# Revit family: FT Excalibur_2021
name_source: partatom
category: Luminarias
units: mm (PartAtom-declared; Revit-internal decimal feet)

## family parameters
Compartido = No
Corte con vacíos al cargar = No
Cota de conector redondo = Diámetro de uso
Número OmniClass = 23.80.70.00
Origen de luz = Sí
Punto de cálculo de habitación = No
Se basa en plano de trabajo = No
Siempre vertical = Sí
Tipo de pieza = Normal
Título OmniClass = Lighting

## types (12) — shared parameters
Cambio de temperatura de color de luz atenuada = <Ninguno>
Chromatic Index = CR>80
Descripción = https://www.airfal.com
Emergency system = No
Filtro de color = 16777215
Glow wire test = 960ºC
IK = IK07
IP = IP67
Led Module = Sí
MacAdam Ellipse = 3/4
Photobiological risk group = RG 0/1
URL = https://www.airfal.com
Unify glade rating = UGR<19
Useful life = L70B50>50000
Ángulo de inclinación = 90.00°
zero-valued in all types: Elevación por defecto

## per-type parameters (varying)
| type | Archivo de red fotométrica | L | Longitud de línea de emisión | Net output | Watts |
| ER113 | ER224 EXCALIBUR 1200 32W 5550 lm G5.IES | 1080 mm  [stored 3.54331 ft] | 1080 mm  [stored 3.54331 ft] | 3247 lm | 32 W |
| ER114 | ER114 EXCALIBUR 600 13W 1550 Lm 4000K.IES | 1080 mm  [stored 3.54331 ft] | 1080 mm  [stored 3.54331 ft] | 942 lm | 13 W |
| ER123 | ER123 EXCALIBUR 600 16W 2650 lm G5.IES | 1080 mm  [stored 3.54331 ft] | 1080 mm  [stored 3.54331 ft] | 1556 lm | 16 W |
| ER124 | ER124 EXCALIBUR 600 16W 2775 lm G5.IES | 1080 mm  [stored 3.54331 ft] | 1080 mm  [stored 3.54331 ft] | 1623 lm | 16 W |
| ER213 | ER213 EXCALIBUR 1200 24W 2980 Lm 3000 K.IES | 1620 mm | 1620 mm | 1812 lm | 24 W |
| ER214 | ER214 EXCALIBUR 1200 24W 3200 Lm 4000 K.IES | 1620 mm | 1620 mm | 1946 lm | 24 W |
| ER223 | ER223 EXCALIBUR 1200 32W 5300 lm G5.IES | 1620 mm | 1620 mm | 3113 lm | 32 W |
| ER224 | ER224 EXCALIBUR 1200 32W 5550 lm G5.IES | 1620 mm | 1620 mm | 3247 lm | 32 W |
| ER313 | ER313 EXCALIBUR 1500 29W 3720 Lm 3000 K.IES | 1910 mm  [stored 6.2664 ft] | 1910 mm  [stored 6.2664 ft] | 2262 lm | 29 W |
| ER314 | ER314 EXCALIBUR 1500 29W 4000 Lm 4000 K.IES | 1910 mm  [stored 6.2664 ft] | 1910 mm  [stored 6.2664 ft] | 2432 lm | 29 W |
| ER323 | ER323 EXCALIBUR 1500 40W 6631 lm G5.IES | 1910 mm  [stored 6.2664 ft] | 1910 mm  [stored 6.2664 ft] | 3836 lm | 40 W |
| ER324 | ER324 EXCALIBUR 1500 40W 6940 lm G5.IES | 1910 mm  [stored 6.2664 ft] | 1910 mm  [stored 6.2664 ft] | 4074 lm | 40 W |

note: [stored X ft] marks values corroborated as IEEE doubles in the binary element streams (Revit-internal decimal feet)

## geometry (parser evidence)
native form markers: Blend x8, Sweep x23
no freeform markers — native parametric forms only
